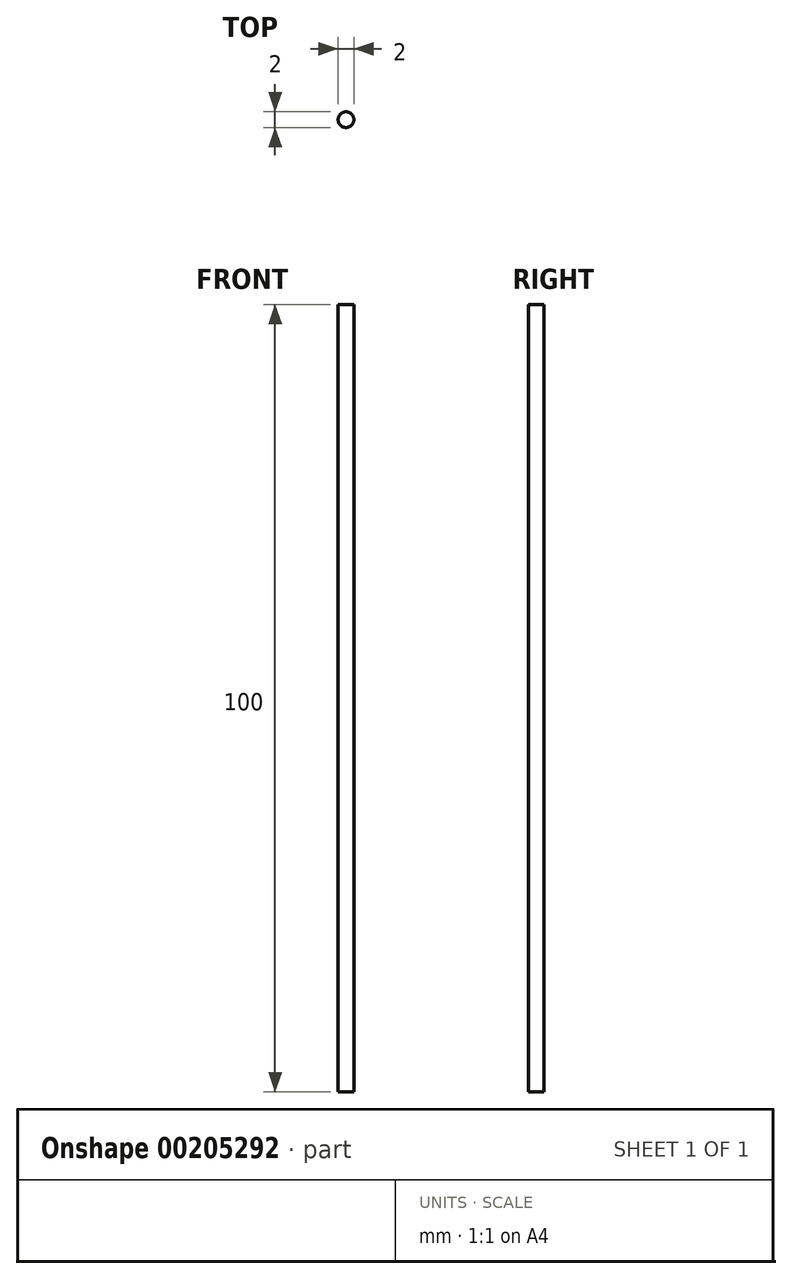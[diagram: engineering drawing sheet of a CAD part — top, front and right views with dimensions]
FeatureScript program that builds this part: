
annotation { "Feature Type Name" : "Feature", "Feature Type Description" : "" }
export const myFeature = defineFeature(function(context is Context, id is Id, definition is map)
    precondition{}
    {
        {
            var Q0;
            Q0=qCreatedBy(makeId("Top.planeOp"),FACE);
            var sketch = newSketch(context, id + "F0", { "sketchPlane" : qUnion([Q0])});
            skCircle(sketch, "E0", {"center": v(0, 0) * mm, "radius": 1 * mm});
            skSolve(sketch);
        }
        {
            var Q0;
            Q0=makeQuery(id+"F0.imprint","IMPRINT",FACE,{"disambiguationData":[TD([[makeQuery(id+"F0.imprint","IMPRINT",EDGE,{"derivedFrom":sQuery(id+"F0.wireOp",EDGE,"E0")}),1.0]])]});
            extrude(context, id + "F1", {"entities" : qUnion([Q0]), "depth" : 100 * mm});
        }
    });
